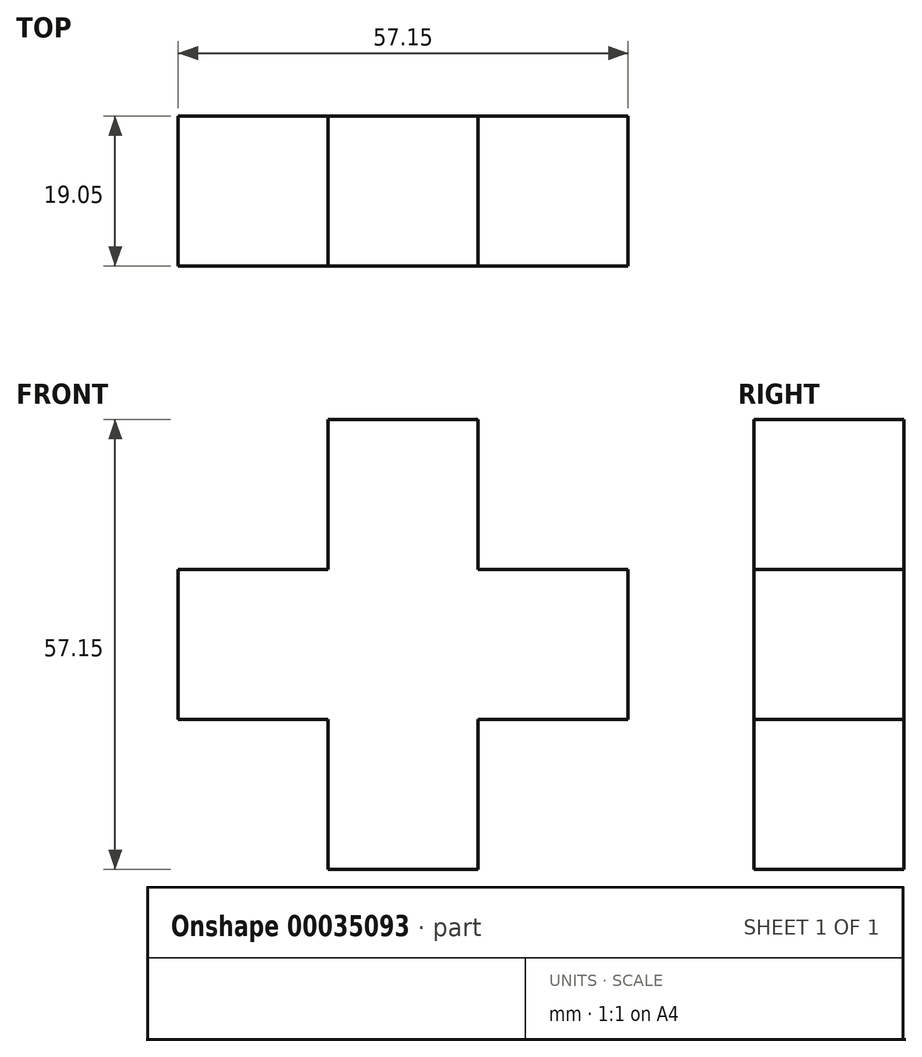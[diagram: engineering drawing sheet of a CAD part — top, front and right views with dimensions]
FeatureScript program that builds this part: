
annotation { "Feature Type Name" : "Feature", "Feature Type Description" : "" }
export const myFeature = defineFeature(function(context is Context, id is Id, definition is map)
    precondition{}
    {
        {
            var Q0;
            Q0=qCreatedBy(makeId("Front.planeOp"),FACE);
            var sketch = newSketch(context, id + "F0", { "sketchPlane" : qUnion([Q0])});
            skLineSegment(sketch, "E0", {"start": v(-19.05, 0) * mm, "end": v(0, 0) * mm});
            skLineSegment(sketch, "E1", {"start": v(0, 0) * mm, "end": v(0, 0) * mm});
            skLineSegment(sketch, "E2", {"start": v(0, 0) * mm, "end": v(19.05, 0) * mm});
            skLineSegment(sketch, "E3", {"start": v(19.05, 0) * mm, "end": v(19.05, -19.05) * mm});
            skLineSegment(sketch, "E4", {"start": v(19.05, -19.05) * mm, "end": v(0, -19.05) * mm});
            skLineSegment(sketch, "E5", {"start": v(0, -19.05) * mm, "end": v(0, -38.1) * mm});
            skLineSegment(sketch, "E6", {"start": v(0, -38.1) * mm, "end": v(-19.05, -38.1) * mm});
            skLineSegment(sketch, "E7", {"start": v(-19.05, -38.1) * mm, "end": v(-19.05, -19.05) * mm});
            skLineSegment(sketch, "E8", {"start": v(-19.05, -19.05) * mm, "end": v(-38.1, -19.05) * mm});
            skLineSegment(sketch, "E9", {"start": v(-38.1, -19.05) * mm, "end": v(-38.1, 0) * mm});
            skLineSegment(sketch, "E10", {"start": v(-38.1, 0) * mm, "end": v(-19.05, 0) * mm});
            skLineSegment(sketch, "E11", {"start": v(-19.05, 0) * mm, "end": v(-19.05, 0) * mm});
            skLineSegment(sketch, "E12", {"start": v(-19.05, 0) * mm, "end": v(-19.05, 19.05) * mm});
            skLineSegment(sketch, "E13", {"start": v(-19.05, 19.05) * mm, "end": v(0, 19.05) * mm});
            skLineSegment(sketch, "E14", {"start": v(0, 19.05) * mm, "end": v(0, 0) * mm});
            skSolve(sketch);
        }
        {
            var Q0;
            Q0 = qSketchRegion(id + "F0", true);
            extrude(context, id + "F1", {"entities" : qUnion([Q0]), "depth" : 19.05 * mm});
        }
    });
